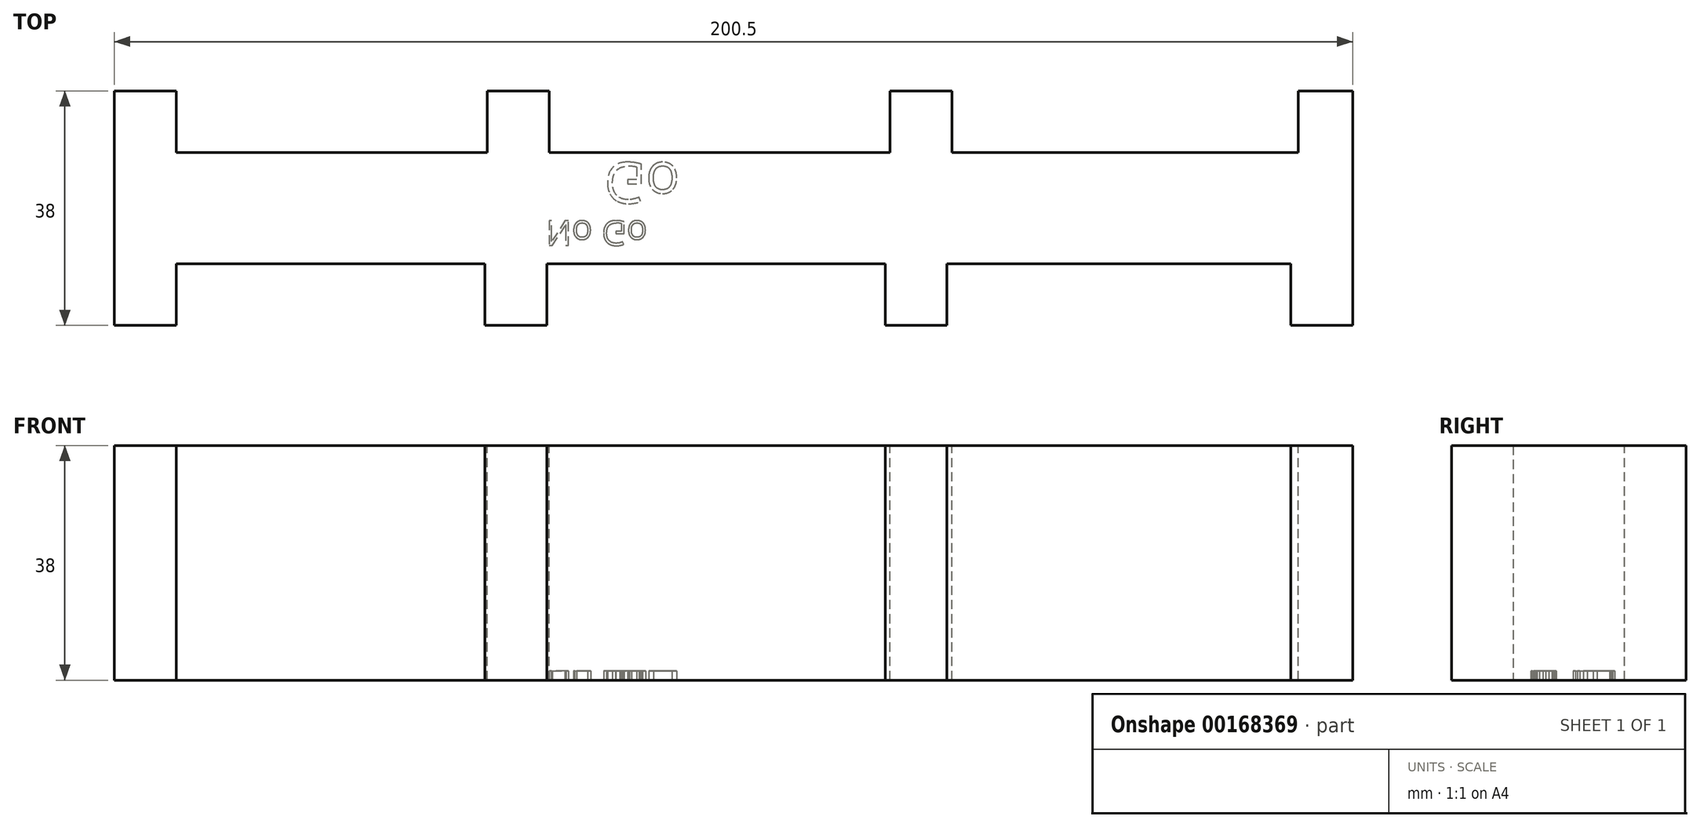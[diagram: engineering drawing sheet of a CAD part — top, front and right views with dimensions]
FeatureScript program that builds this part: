
annotation { "Feature Type Name" : "Feature", "Feature Type Description" : "" }
export const myFeature = defineFeature(function(context is Context, id is Id, definition is map)
    precondition{}
    {
        {
            var Q0;
            Q0=qCreatedBy(makeId("Front.planeOp"),FACE);
            var sketch = newSketch(context, id + "F0", { "sketchPlane" : qUnion([Q0])});
            skLineSegment(sketch, "E0.bottom", {"start": v(0, 0) * mm, "end": v(200.5, 0) * mm});
            skLineSegment(sketch, "E0.top", {"start": v(0, -38) * mm, "end": v(200.5, -38) * mm});
            skLineSegment(sketch, "E0.left", {"start": v(0, 0) * mm, "end": v(0, -38) * mm});
            skLineSegment(sketch, "E0.right", {"start": v(200.5, 0) * mm, "end": v(200.5, -38) * mm});
            skSolve(sketch);
        }
        {
            var Q0;
            Q0=makeQuery(id+"F0.imprint","IMPRINT",FACE,{"disambiguationData":[TD([[makeQuery(id+"F0.imprint","IMPRINT",EDGE,{"derivedFrom":sQuery(id+"F0.wireOp",EDGE,"E0.bottom")}),-1.0]])]});
            extrude(context, id + "F1", {"entities" : qUnion([Q0]), "depth" : 38 * mm});
        }
        {
            var Q0;
            Q0=makeQuery(id+"F1.opExtrude","CAP_FACE",FACE,{"disambiguationData":[OSD([sQuery(id+"F0.wireOp",EDGE,"E0.bottom"),sQuery(id+"F0.wireOp",EDGE,"E0.top"),sQuery(id+"F0.wireOp",EDGE,"E0.left"),sQuery(id+"F0.wireOp",EDGE,"E0.right")])],"isStart":false});
            var sketch = newSketch(context, id + "F2", { "sketchPlane" : qUnion([Q0])});
            skLineSegment(sketch, "E1.bottom", {"start": v(10, 0) * mm, "end": v(60, 0) * mm});
            skLineSegment(sketch, "E1.top", {"start": v(10, -38) * mm, "end": v(60, -38) * mm});
            skLineSegment(sketch, "E1.left", {"start": v(10, 0) * mm, "end": v(10, -38) * mm});
            skLineSegment(sketch, "E1.right", {"start": v(60, 0) * mm, "end": v(60, -38) * mm});
            skLineSegment(sketch, "E2.bottom", {"start": v(70, 0) * mm, "end": v(124.8, 0) * mm});
            skLineSegment(sketch, "E2.top", {"start": v(70, -38) * mm, "end": v(124.8, -38) * mm});
            skLineSegment(sketch, "E2.left", {"start": v(70, 0) * mm, "end": v(70, -38) * mm});
            skLineSegment(sketch, "E2.right", {"start": v(124.8, 0) * mm, "end": v(124.8, -38) * mm});
            skLineSegment(sketch, "E3.bottom", {"start": v(134.8, 0) * mm, "end": v(190.5, 0) * mm});
            skLineSegment(sketch, "E3.top", {"start": v(134.8, -38) * mm, "end": v(190.5, -38) * mm});
            skLineSegment(sketch, "E3.left", {"start": v(134.8, 0) * mm, "end": v(134.8, -38) * mm});
            skLineSegment(sketch, "E3.right", {"start": v(190.5, 0) * mm, "end": v(190.5, -38) * mm});
            skSolve(sketch);
        }
        {
            var Q0;
            Q0=makeQuery(id+"F2.imprint","IMPRINT",FACE,{"disambiguationData":[TD([[makeQuery(id+"F2.imprint","IMPRINT",EDGE,{"derivedFrom":sQuery(id+"F2.wireOp",EDGE,"E3.bottom")}),-1.0]])]});
            var Q1;
            Q1=makeQuery(id+"F2.imprint","IMPRINT",FACE,{"disambiguationData":[TD([[makeQuery(id+"F2.imprint","IMPRINT",EDGE,{"derivedFrom":sQuery(id+"F2.wireOp",EDGE,"E2.bottom")}),-1.0]])]});
            var Q2;
            Q2=makeQuery(id+"F2.imprint","IMPRINT",FACE,{"disambiguationData":[TD([[makeQuery(id+"F2.imprint","IMPRINT",EDGE,{"derivedFrom":sQuery(id+"F2.wireOp",EDGE,"E1.bottom")}),-1.0]])]});
            extrude(context, id + "F3", {"entities" : qUnion([Q0, Q1, Q2]), "operationType" : NewBodyOperationType.REMOVE, "oppositeDirection" : true, "depth" : 10 * mm});
        }
        {
            var Q0;
            Q0=makeQuery(id+"F1.opExtrude","CAP_FACE",FACE,{"disambiguationData":[OSD([sQuery(id+"F0.wireOp",EDGE,"E0.bottom"),sQuery(id+"F0.wireOp",EDGE,"E0.top"),sQuery(id+"F0.wireOp",EDGE,"E0.left"),sQuery(id+"F0.wireOp",EDGE,"E0.right")])],"isStart":true});
            var sketch = newSketch(context, id + "F4", { "sketchPlane" : qUnion([Q0])});
            skLineSegment(sketch, "E4.bottom", {"start": v(-10, -38) * mm, "end": v(-60.4, -38) * mm});
            skLineSegment(sketch, "E4.top", {"start": v(-10, 0) * mm, "end": v(-60.4, 0) * mm});
            skLineSegment(sketch, "E4.left", {"start": v(-10, -38) * mm, "end": v(-10, 0) * mm});
            skLineSegment(sketch, "E4.right", {"start": v(-60.4, -38) * mm, "end": v(-60.4, 0) * mm});
            skLineSegment(sketch, "E5.bottom", {"start": v(-70.4, -38) * mm, "end": v(-125.6, -38) * mm});
            skLineSegment(sketch, "E5.top", {"start": v(-70.4, 0) * mm, "end": v(-125.6, 0) * mm});
            skLineSegment(sketch, "E5.left", {"start": v(-70.4, -38) * mm, "end": v(-70.4, 0) * mm});
            skLineSegment(sketch, "E5.right", {"start": v(-125.6, -38) * mm, "end": v(-125.6, 0) * mm});
            skLineSegment(sketch, "E6.bottom", {"start": v(-135.6, -38) * mm, "end": v(-191.7, -38) * mm});
            skLineSegment(sketch, "E6.top", {"start": v(-135.6, 0.13) * mm, "end": v(-191.7, 0.13) * mm});
            skLineSegment(sketch, "E6.left", {"start": v(-135.6, -38) * mm, "end": v(-135.6, 0.13) * mm});
            skLineSegment(sketch, "E6.right", {"start": v(-191.7, -38) * mm, "end": v(-191.7, 0.13) * mm});
            skSolve(sketch);
        }
        {
            var Q0;
            Q0 = qSketchRegion(id + "F4", true);
            extrude(context, id + "F5", {"entities" : qUnion([Q0]), "operationType" : NewBodyOperationType.REMOVE, "oppositeDirection" : true, "depth" : 10 * mm});
        }
        {
            var Q0;
            Q0=makeQuery(id+"F1.opExtrude","SWEPT_FACE",FACE,{"disambiguationData":[OSD([sQuery(id+"F0.wireOp",EDGE,"E0.top")])]});
            var sketch = newSketch(context, id + "F6", { "sketchPlane" : qUnion([Q0])});
            skText(sketch, "E7", { "text": "No Go", "fontName": "OpenSans-Regular.ttf"});
            skText(sketch, "E8", { "text": "Go", "fontName": "OpenSans-Regular.ttf"});
            const initialGuessF6  = {"E7": [0.06984, 0.02107, 1, 0, 0.00402], "E8": [0.07928, 0.01163, 1, 0, 0.00664]};
            skSetInitialGuess(sketch, initialGuessF6);
            skSolve(sketch);
        }
        {
            var Q0;
            Q0 = qSketchRegion(id + "F6", true);
            extrude(context, id + "F7", {"entities" : qUnion([Q0]), "operationType" : NewBodyOperationType.REMOVE, "oppositeDirection" : true, "depth" : 1.5 * mm});
        }
    });
